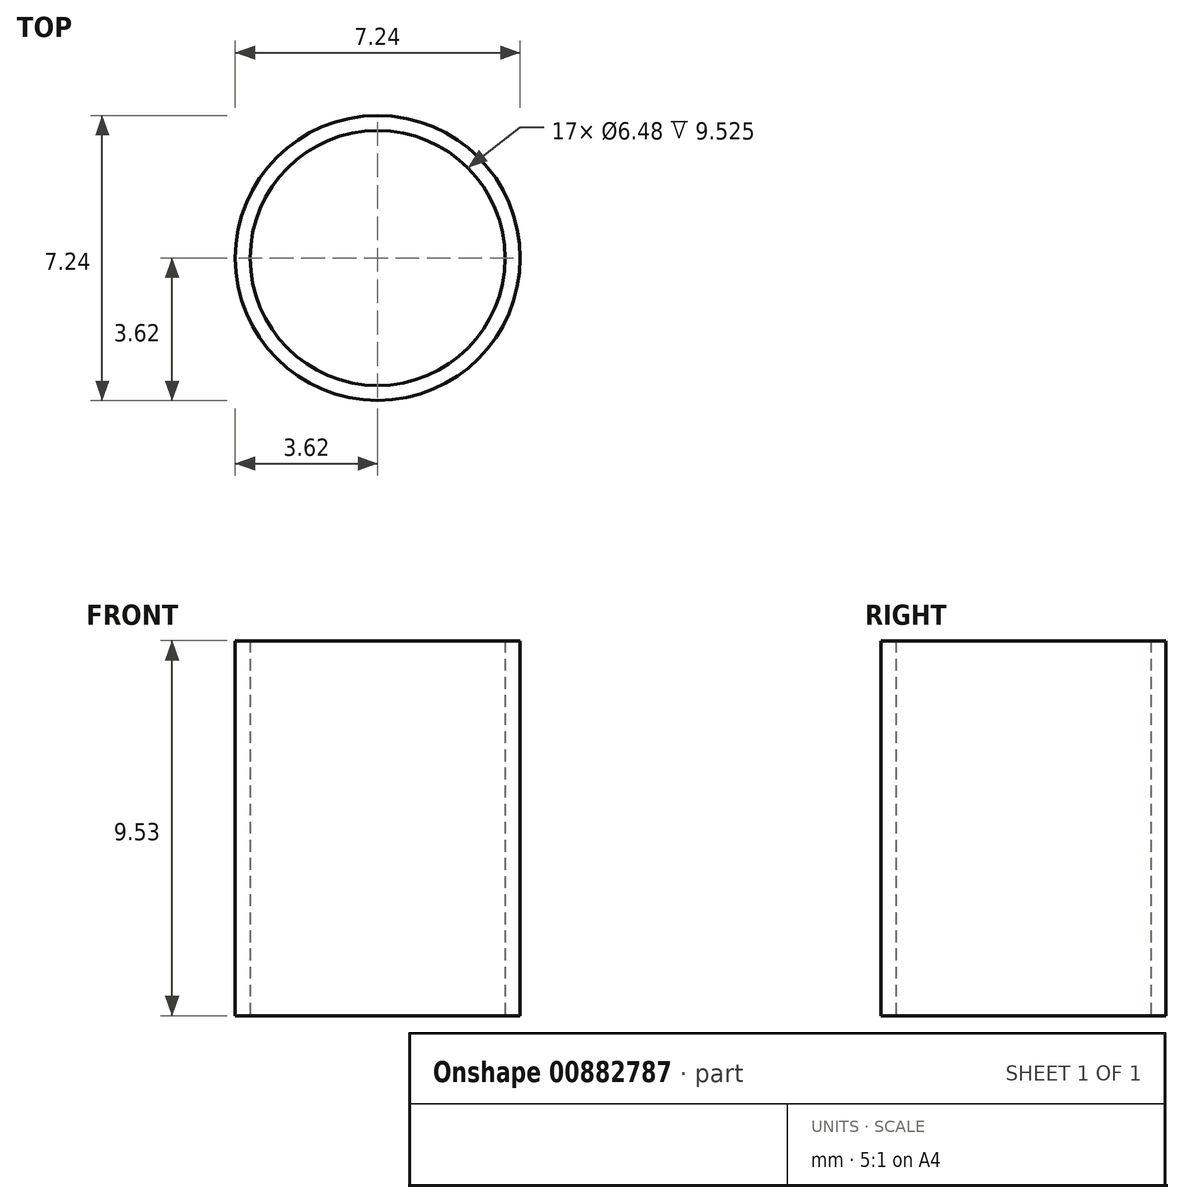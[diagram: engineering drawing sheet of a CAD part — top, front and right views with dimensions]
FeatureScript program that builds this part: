
annotation { "Feature Type Name" : "Feature", "Feature Type Description" : "" }
export const myFeature = defineFeature(function(context is Context, id is Id, definition is map)
    precondition{}
    {
        {
            var Q0;
            Q0=qCreatedBy(makeId("Top.planeOp"),FACE);
            var sketch = newSketch(context, id + "F0", { "sketchPlane" : qUnion([Q0])});
            skCircle(sketch, "E0", {"center": v(0, 0) * mm, "radius": 3.24 * mm});
            skCircle(sketch, "E1", {"center": v(0, 0) * mm, "radius": 3.62 * mm});
            skSolve(sketch);
        }
        {
            var Q0;
            Q0 = qSketchRegion(id + "F0", true);
            extrude(context, id + "F1", {"entities" : qUnion([Q0]), "depth" : 9.52 * mm, "offsetDistance" : 25.4 * mm});
        }
    });
